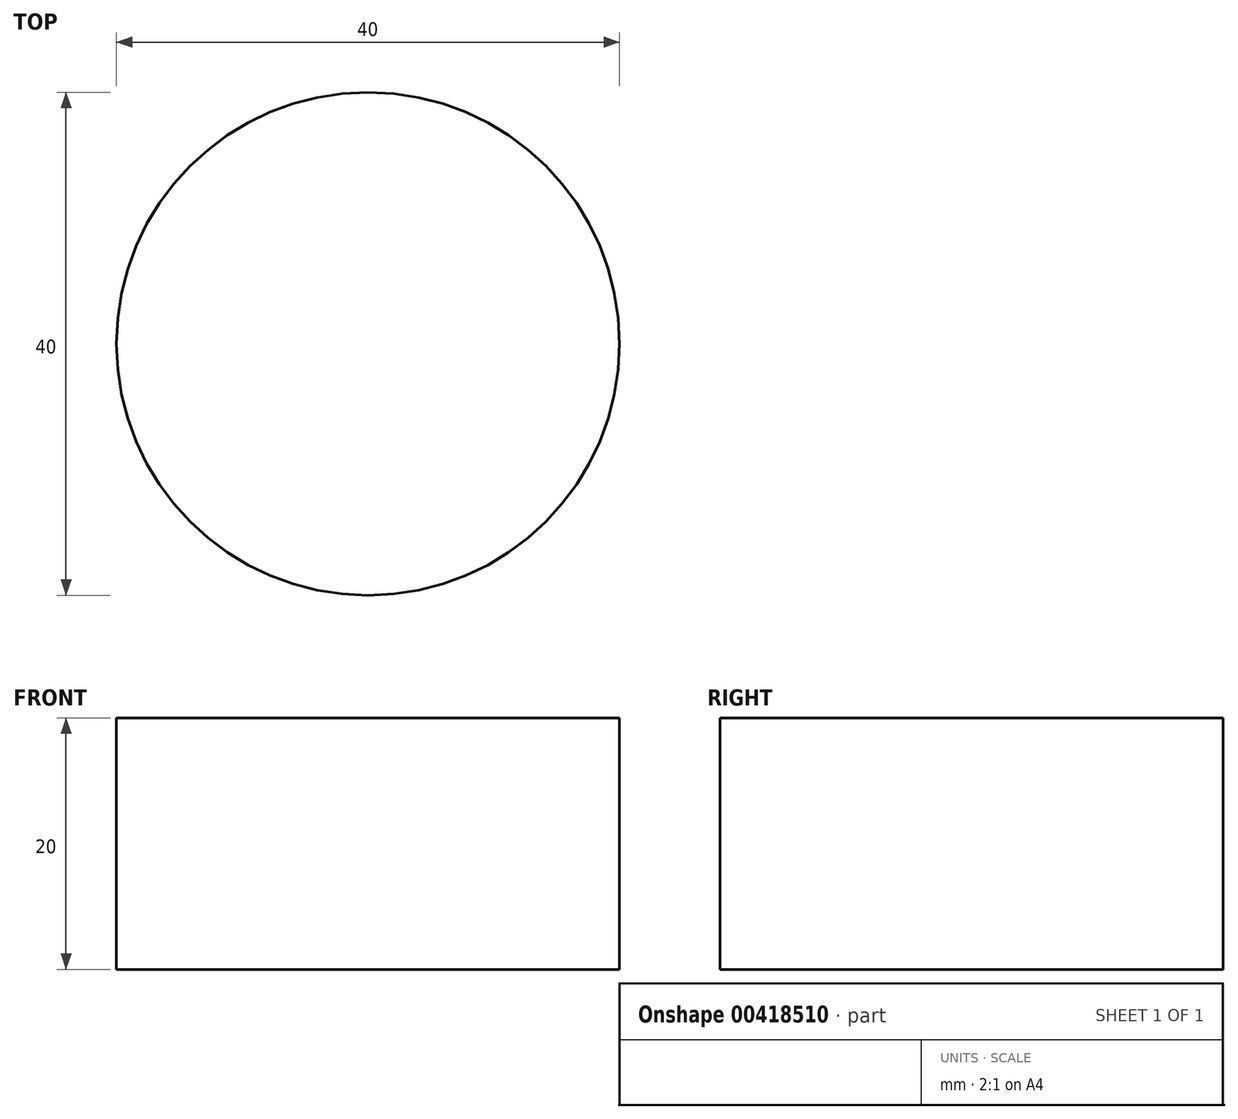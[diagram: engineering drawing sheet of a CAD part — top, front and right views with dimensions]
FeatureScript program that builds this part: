
annotation { "Feature Type Name" : "Feature", "Feature Type Description" : "" }
export const myFeature = defineFeature(function(context is Context, id is Id, definition is map)
    precondition{}
    {
        {
            var Q0;
            Q0=qCreatedBy(makeId("Top.planeOp"),FACE);
            var sketch = newSketch(context, id + "F0", { "sketchPlane" : qUnion([Q0])});
            skCircle(sketch, "E0", {"center": v(0, 0) * mm, "radius": 20 * mm});
            skSolve(sketch);
        }
        {
            var Q0;
            Q0=makeQuery(id+"F0.imprint","IMPRINT",FACE,{"disambiguationData":[TD([[makeQuery(id+"F0.imprint","IMPRINT",EDGE,{"derivedFrom":sQuery(id+"F0.wireOp",EDGE,"E0")}),1.0]])]});
            extrude(context, id + "F1", {"entities" : qUnion([Q0]), "depth" : 20 * mm});
        }
    });
